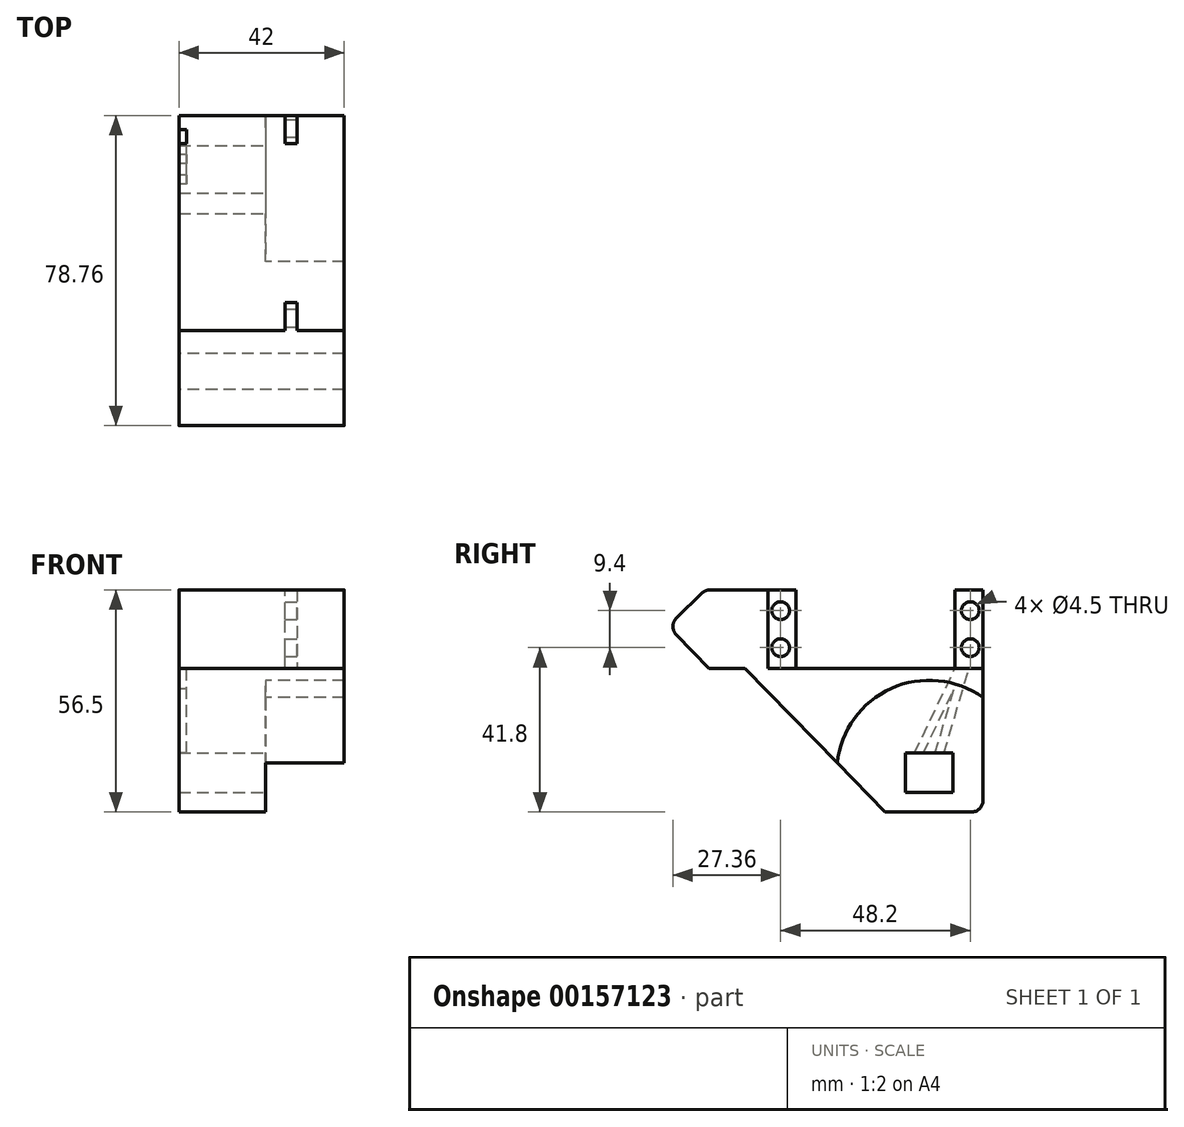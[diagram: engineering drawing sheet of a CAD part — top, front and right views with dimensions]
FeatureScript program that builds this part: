
annotation { "Feature Type Name" : "Feature", "Feature Type Description" : "" }
export const myFeature = defineFeature(function(context is Context, id is Id, definition is map)
    precondition{}
    {
        {
            var Q0;
            Q0=qCreatedBy(makeId("Right.planeOp"),FACE);
            var sketch = newSketch(context, id + "F0", { "sketchPlane" : qUnion([Q0])});
            skLineSegment(sketch, "E0", {"start": v(27.3, -32.2) * mm, "end": v(27.3, 1.3) * mm});
            skLineSegment(sketch, "E1.bottom", {"start": v(19.65, -20.2) * mm, "end": v(7.65, -20.2) * mm});
            skLineSegment(sketch, "E1.top", {"start": v(19.65, -30.2) * mm, "end": v(7.65, -30.2) * mm});
            skLineSegment(sketch, "E1.left", {"start": v(19.65, -20.2) * mm, "end": v(19.65, -30.2) * mm});
            skLineSegment(sketch, "E1.right", {"start": v(7.65, -20.2) * mm, "end": v(7.65, -30.2) * mm});
            skLineSegment(sketch, "E2", {"start": v(7.65, -20.2) * mm, "end": v(19.65, -30.2) * mm, "construction": true});
            skLineSegment(sketch, "E3", {"start": v(13.65, -30.2) * mm, "end": v(13.65, -35.2) * mm, "construction": true});
            skLineSegment(sketch, "E4", {"start": v(27.3, 1.3) * mm, "end": v(27.3, 1.3) * mm});
            skPoint(sketch, "E5.endSnap0", {"position": v(13.65, -32.7) * mm});
            skCircle(sketch, "E6", {"center": v(13.65, -25.2) * mm, "radius": 21.5 * mm, "construction": true});
            skPoint(sketch, "E7.visualSharp", {"position": v(27.3, -35.2) * mm});
            skArc(sketch, "E7.filletArc", {"start": v(24.3, -35.2) * mm, "mid": v(26.42, -34.33) * mm, "end": v(27.3, -32.2) * mm});
            skArc(sketch, "E8", {"start": v(27.3, -6.08) * mm, "mid": v(4, -3.78) * mm, "end": v(-9.72, -22.76) * mm});
            skPoint(sketch, "E9.MirrorCS.end.orphan", {"position": v(0, -6) * mm});
            skLineSegment(sketch, "E10", {"start": v(-27.3, 1.3) * mm, "end": v(27.3, 1.3) * mm});
            skLineSegment(sketch, "E11", {"start": v(7.65, -20.2) * mm, "end": v(13.65, -20.2) * mm, "construction": true});
            skLineSegment(sketch, "E12", {"start": v(13.65, -20.2) * mm, "end": v(13.65, 1.3) * mm, "construction": true});
            skLineSegment(sketch, "E13", {"start": v(13.65, 1.3) * mm, "end": v(13.65, -1.7) * mm, "construction": true});
            skLineSegment(sketch, "E14", {"start": v(27.3, 1.3) * mm, "end": v(20.2, 1.3) * mm});
            skLineSegment(sketch, "E15", {"start": v(20.2, 1.3) * mm, "end": v(20.2, 21.3) * mm});
            skLineSegment(sketch, "E16", {"start": v(20.2, 21.3) * mm, "end": v(27.3, 21.3) * mm});
            skLineSegment(sketch, "E17", {"start": v(27.3, 21.3) * mm, "end": v(27.3, 1.3) * mm});
            skLineSegment(sketch, "E18", {"start": v(-27.3, 1.3) * mm, "end": v(-27.3, 21.3) * mm});
            skLineSegment(sketch, "E19", {"start": v(-27.3, 21.3) * mm, "end": v(-20.2, 21.3) * mm});
            skLineSegment(sketch, "E20", {"start": v(-20.2, 21.3) * mm, "end": v(-20.2, 1.3) * mm});
            skLineSegment(sketch, "E21", {"start": v(-20.2, 1.3) * mm, "end": v(-27.3, 1.3) * mm});
            skLineSegment(sketch, "E22", {"start": v(-20.2, 1.3) * mm, "end": v(-24.1, 1.3) * mm, "construction": true});
            skLineSegment(sketch, "E23", {"start": v(-24.1, 1.3) * mm, "end": v(-24.1, 21.3) * mm, "construction": true});
            skLineSegment(sketch, "E24", {"start": v(20.2, 1.3) * mm, "end": v(24.1, 1.3) * mm, "construction": true});
            skLineSegment(sketch, "E25", {"start": v(24.1, 1.3) * mm, "end": v(24.1, 21.3) * mm, "construction": true});
            skLineSegment(sketch, "E26", {"start": v(-24.1, 1.3) * mm, "end": v(-24.1, 6.6) * mm, "construction": true});
            skLineSegment(sketch, "E27", {"start": v(-24.1, 6.6) * mm, "end": v(-24.1, 16) * mm, "construction": true});
            skLineSegment(sketch, "E28", {"start": v(24.1, 1.3) * mm, "end": v(24.1, 6.6) * mm, "construction": true});
            skLineSegment(sketch, "E29", {"start": v(24.1, 6.6) * mm, "end": v(24.1, 16) * mm, "construction": true});
            skCircle(sketch, "E30", {"center": v(-24.1, 16) * mm, "radius": 2.25 * mm});
            skCircle(sketch, "E31", {"center": v(-24.1, 6.6) * mm, "radius": 2.25 * mm});
            skCircle(sketch, "E32", {"center": v(24.1, 6.6) * mm, "radius": 2.25 * mm});
            skCircle(sketch, "E33", {"center": v(24.1, 16) * mm, "radius": 2.25 * mm});
            skLineSegment(sketch, "E34", {"start": v(24.3, -35.2) * mm, "end": v(2.43, -35.2) * mm});
            skLineSegment(sketch, "E35", {"start": v(20.2, 21.3) * mm, "end": v(10.1, 21.3) * mm, "construction": true});
            skLineSegment(sketch, "E36", {"start": v(10.1, 21.3) * mm, "end": v(10.1, 1.3) * mm, "construction": true});
            skLineSegment(sketch, "E37", {"start": v(-24.1, 11.3) * mm, "end": v(24.1, 11.3) * mm, "construction": true});
            skLineSegment(sketch, "E38", {"start": v(13.65, -35.2) * mm, "end": v(13.65, -46.7) * mm, "construction": true});
            skLineSegment(sketch, "E39", {"start": v(-33.19, 1.3) * mm, "end": v(2.43, -35.2) * mm});
            skLineSegment(sketch, "E40", {"start": v(-27.3, 1.3) * mm, "end": v(-42.25, 1.3) * mm});
            skLineSegment(sketch, "E41", {"start": v(-42.25, 1.3) * mm, "end": v(13.2, -55.54) * mm, "construction": true});
            skPoint(sketch, "E42.second.point", {"position": v(-2.1, -5.74) * mm});
            skPoint(sketch, "E42.third.point", {"position": v(-11.7, -30.01) * mm});
            skArc(sketch, "E43.trimOffspring", {"start": v(-14.8, -17.55) * mm, "mid": v(-10.87, -30.94) * mm, "end": v(2.43, -35.2) * mm});
            skLineSegment(sketch, "E44", {"start": v(-27.3, 21.3) * mm, "end": v(-41.96, 21.3) * mm});
            skLineSegment(sketch, "E45", {"start": v(-42.25, 1.3) * mm, "end": v(-50.6, 9.86) * mm});
            skLineSegment(sketch, "E46", {"start": v(-50.55, 14.1) * mm, "end": v(-44.06, 20.44) * mm});
            skLineSegment(sketch, "E47", {"start": v(-33.19, 1.3) * mm, "end": v(-47.94, 16.41) * mm});
            skPoint(sketch, "E48.visualSharp", {"position": v(-43.18, 21.3) * mm});
            skArc(sketch, "E48.filletArc", {"start": v(-41.96, 21.3) * mm, "mid": v(-43.1, 21.07) * mm, "end": v(-44.06, 20.44) * mm});
            skPoint(sketch, "E49.visualSharp", {"position": v(-52.7, 12) * mm});
            skArc(sketch, "E49.filletArc", {"start": v(-50.55, 14.1) * mm, "mid": v(-51.46, 11.99) * mm, "end": v(-50.6, 9.86) * mm});
            skSolve(sketch);
        }
        {
            var Q0;
            {var subQ6=sQuery(id+"F0.wireOp",EDGE,"E8");Q0=makeQuery(id+"F0.imprint","IMPRINT",FACE,{"disambiguationData":[TD([[makeQuery(id+"F0.imprint","IMPRINT",EDGE,{"derivedFrom":subQ6}),-1.0]])]});}
            var Q1;
            {var subQ2=sQuery(id+"F0.wireOp",EDGE,"E18");Q1=makeQuery(id+"F0.imprint","IMPRINT",FACE,{"disambiguationData":[TD([[makeQuery(id+"F0.imprint","IMPRINT",EDGE,{"derivedFrom":subQ2}),1.0]])]});}
            extrude(context, id + "F1", {"entities" : qUnion([Q0, Q1]), "depth" : 20 * mm});
        }
        {
            var Q0;
            {var subQ6=sQuery(id+"F0.wireOp",EDGE,"E8");Q0=makeQuery(id+"F0.imprint","IMPRINT",FACE,{"disambiguationData":[TD([[makeQuery(id+"F0.imprint","IMPRINT",EDGE,{"derivedFrom":subQ6}),-1.0]])]});}
            var Q1;
            Q1=makeQuery(id+"F0.imprint","IMPRINT",FACE,{"disambiguationData":[TD([[makeQuery(id+"F0.imprint","IMPRINT",EDGE,{"derivedFrom":sQuery(id+"F0.wireOp",EDGE,"E1.bottom")}),-1.0]])]});
            var Q2;
            {var subQ2=sQuery(id+"F0.wireOp",EDGE,"E18");Q2=makeQuery(id+"F0.imprint","IMPRINT",FACE,{"disambiguationData":[TD([[makeQuery(id+"F0.imprint","IMPRINT",EDGE,{"derivedFrom":subQ2}),1.0]])]});}
            extrude(context, id + "F2", {"entities" : qUnion([Q0, Q1, Q2]), "operationType" : NewBodyOperationType.ADD, "oppositeDirection" : true, "depth" : 20 * mm});
        }
        {
            var Q0;
            Q0=makeQuery(id+"F2.opExtrude","CAP_FACE",FACE,{"disambiguationData":[OSD([sQuery(id+"F0.wireOp",EDGE,"E0"),sQuery(id+"F0.wireOp",EDGE,"E1.bottom"),sQuery(id+"F0.wireOp",EDGE,"E1.top"),sQuery(id+"F0.wireOp",EDGE,"E1.left"),sQuery(id+"F0.wireOp",EDGE,"E1.right"),sQuery(id+"F0.wireOp",EDGE,"E7.filletArc"),sQuery(id+"F0.wireOp",EDGE,"E10"),sQuery(id+"F0.wireOp",EDGE,"E14"),sQuery(id+"F0.wireOp",EDGE,"E18"),sQuery(id+"F0.wireOp",EDGE,"E21"),sQuery(id+"F0.wireOp",EDGE,"E34"),sQuery(id+"F0.wireOp",EDGE,"Nva1be2E-KNAd-LMN7-Fm0M-Tev44zCaLiBh"),sQuery(id+"F0.wireOp",EDGE,"E39"),sQuery(id+"F0.wireOp",EDGE,"xTKFIYey-ZxMZ-6zIN-Clns-HEuuajznrW0n"),sQuery(id+"F0.wireOp",EDGE,"E40"),sQuery(id+"F0.wireOp",EDGE,"7Onhy3Lj-w6oU-KviF-Unfc-9GFb9hkfj7ZY")])],"isStart":false});
            var sketch = newSketch(context, id + "F3", { "sketchPlane" : qUnion([Q0])});
            skLineSegment(sketch, "E50.0", {"start": v(-19.65, -20.2) * mm, "end": v(-7.65, -20.2) * mm});
            skLineSegment(sketch, "E50.1", {"start": v(-19.65, -20.2) * mm, "end": v(-19.65, -30.2) * mm});
            skLineSegment(sketch, "E50.2", {"start": v(-7.65, -20.2) * mm, "end": v(-7.65, -30.2) * mm});
            skLineSegment(sketch, "E50.3", {"start": v(-19.65, -30.2) * mm, "end": v(-7.65, -30.2) * mm});
            skLineSegment(sketch, "E51", {"start": v(-13.65, -20.2) * mm, "end": v(-12.15, -20.2) * mm});
            skLineSegment(sketch, "E52", {"start": v(-12.15, -20.2) * mm, "end": v(-12.15, -30.2) * mm});
            skLineSegment(sketch, "E53", {"start": v(-12.15, -30.2) * mm, "end": v(-15.15, -30.2) * mm});
            skLineSegment(sketch, "E54", {"start": v(-15.15, -30.2) * mm, "end": v(-15.15, -20.2) * mm});
            skArc(sketch, "E55.0", {"start": v(14.8, -17.55) * mm, "mid": v(10.87, -30.94) * mm, "end": v(-2.43, -35.2) * mm});
            skSolve(sketch);
        }
        {
            var Q0;
            {var subQ0=sQuery(id+"F3.wireOp",EDGE,"E55.0");Q0=makeQuery(id+"F3.imprint","IMPRINT",FACE,{"disambiguationData":[TD([[makeQuery(id+"F3.imprint","IMPRINT",EDGE,{"derivedFrom":subQ0}),-1.0]])]});}
            var Q1;
            {var subQ0=sQuery(id+"F3.wireOp",EDGE,"E51");Q1=makeQuery(id+"F3.imprint","IMPRINT",FACE,{"disambiguationData":[TD([[makeQuery(id+"F3.imprint","IMPRINT",EDGE,{"derivedFrom":subQ0}),-1.0]])]});}
            var Q2;
            {var subQ5=sQuery(id+"F3.wireOp",EDGE,"E50.1");Q2=makeQuery(id+"F3.imprint","IMPRINT",FACE,{"disambiguationData":[TD([[makeQuery(id+"F3.imprint","IMPRINT",EDGE,{"derivedFrom":subQ5}),-1.0]])]});}
            extrude(context, id + "F4", {"entities" : qUnion([Q0, Q1, Q2]), "operationType" : NewBodyOperationType.ADD, "depth" : 2 * mm});
        }
        {
            var Q0;
            Q0=makeQuery(id+"F1.opExtrude","CAP_FACE",FACE,{"disambiguationData":[OSD([sQuery(id+"F0.wireOp",EDGE,"E0"),sQuery(id+"F0.wireOp",EDGE,"E8"),sQuery(id+"F0.wireOp",EDGE,"E10"),sQuery(id+"F0.wireOp",EDGE,"E14"),sQuery(id+"F0.wireOp",EDGE,"E18"),sQuery(id+"F0.wireOp",EDGE,"E21"),sQuery(id+"F0.wireOp",EDGE,"Nva1be2E-KNAd-LMN7-Fm0M-Tev44zCaLiBh"),sQuery(id+"F0.wireOp",EDGE,"E39"),sQuery(id+"F0.wireOp",EDGE,"xTKFIYey-ZxMZ-6zIN-Clns-HEuuajznrW0n"),sQuery(id+"F0.wireOp",EDGE,"E40"),sQuery(id+"F0.wireOp",EDGE,"7Onhy3Lj-w6oU-KviF-Unfc-9GFb9hkfj7ZY")])],"isStart":false});
            var sketch = newSketch(context, id + "F5", { "sketchPlane" : qUnion([Q0])});
            skSolve(sketch);
        }
        {
            var Q0;
            Q0=makeQuery(id+"F5.imprint","IMPRINT",FACE,{"disambiguationData":[TD([[makeQuery(id+"F5.imprint","IMPRINT",EDGE,{"derivedFrom":makeQuery(id+"F1.opExtrude","CAP_EDGE",EDGE,{"disambiguationData":[OSD([sQuery(id+"F0.wireOp",EDGE,"E0")])],"isStart":false})}),1.0]])]});
            cPlane(context, id + "F6", {"entities" : qUnion([Q0]), "cplaneType" : CPlaneType.OFFSET, "offset" : 12 * mm, "oppositeDirection" : true, "width" : 150 * mm, "height" : 150 * mm});
        }
        {
            var Q0;
            Q0=qCreatedBy(id+"F6.planeOp",FACE);
            var sketch = newSketch(context, id + "F7", { "sketchPlane" : qUnion([Q0])});
            skLineSegment(sketch, "E56.0.0", {"start": v(-27.3, 21.3) * mm, "end": v(-27.3, 1.3) * mm});
            skLineSegment(sketch, "E56.0.1", {"start": v(-27.3, 1.3) * mm, "end": v(-20.2, 1.3) * mm});
            skLineSegment(sketch, "E56.0.2", {"start": v(-20.2, 1.3) * mm, "end": v(-20.2, 21.3) * mm});
            skLineSegment(sketch, "E56.0.3", {"start": v(-20.2, 21.3) * mm, "end": v(-27.3, 21.3) * mm});
            skLineSegment(sketch, "E57.0.0", {"start": v(20.2, 1.3) * mm, "end": v(27.3, 1.3) * mm});
            skLineSegment(sketch, "E57.0.1", {"start": v(27.3, 1.3) * mm, "end": v(27.3, 21.3) * mm});
            skLineSegment(sketch, "E57.0.2", {"start": v(27.3, 21.3) * mm, "end": v(20.2, 21.3) * mm});
            skLineSegment(sketch, "E57.0.3", {"start": v(20.2, 21.3) * mm, "end": v(20.2, 1.3) * mm});
            skLineSegment(sketch, "E58.0", {"start": v(-24.1, 1.3) * mm, "end": v(-24.1, 21.3) * mm});
            skCircle(sketch, "E58.1", {"center": v(-24.1, 16) * mm, "radius": 2.25 * mm});
            skCircle(sketch, "E58.2", {"center": v(-24.1, 6.6) * mm, "radius": 2.25 * mm});
            skLineSegment(sketch, "E58.3", {"start": v(24.1, 1.3) * mm, "end": v(24.1, 21.3) * mm});
            skCircle(sketch, "E58.4", {"center": v(24.1, 6.6) * mm, "radius": 2.25 * mm});
            skCircle(sketch, "E58.5", {"center": v(24.1, 16) * mm, "radius": 2.25 * mm});
            skSolve(sketch);
        }
        {
            var Q0;
            Q0=qSketchRegion(id+"F7",true);
            extrude(context, id + "F8", {"entities" : qUnion([Q0]), "operationType" : NewBodyOperationType.ADD, "oppositeDirection" : true, "depth" : 3 * mm});
        }
        {
            var Q0;
            Q0=makeQuery(id+"F4.opExtrude","CAP_FACE",FACE,{"disambiguationData":[OSD([sQuery(id+"F0.wireOp",EDGE,"E0"),sQuery(id+"F0.wireOp",EDGE,"E7.filletArc"),sQuery(id+"F0.wireOp",EDGE,"E10"),sQuery(id+"F0.wireOp",EDGE,"E14"),sQuery(id+"F0.wireOp",EDGE,"E18"),sQuery(id+"F0.wireOp",EDGE,"E21"),sQuery(id+"F0.wireOp",EDGE,"E34"),sQuery(id+"F0.wireOp",EDGE,"E39"),sQuery(id+"F0.wireOp",EDGE,"E40"),sQuery(id+"F0.wireOp",EDGE,"E44"),sQuery(id+"F0.wireOp",EDGE,"E45"),sQuery(id+"F0.wireOp",EDGE,"E46"),sQuery(id+"F0.wireOp",EDGE,"E48.filletArc"),sQuery(id+"F0.wireOp",EDGE,"E49.filletArc"),sQuery(id+"F3.wireOp",EDGE,"E50.0"),sQuery(id+"F3.wireOp",EDGE,"E50.1"),sQuery(id+"F3.wireOp",EDGE,"E50.2"),sQuery(id+"F3.wireOp",EDGE,"E50.3"),sQuery(id+"F3.wireOp",EDGE,"E52"),sQuery(id+"F3.wireOp",EDGE,"E54"),sQuery(id+"F3.wireOp",EDGE,"E55.0")])],"isStart":false});
            var sketch = newSketch(context, id + "F9", { "sketchPlane" : qUnion([Q0])});
            skLineSegment(sketch, "E59.0", {"start": v(-12.15, -20.2) * mm, "end": v(-9.9, -20.2) * mm});
            skLineSegment(sketch, "E59.1", {"start": v(-17.4, -20.2) * mm, "end": v(-15.15, -20.2) * mm});
            skLineSegment(sketch, "E60.1", {"start": v(-23.75, 1.3) * mm, "end": v(-20.2, 1.3) * mm});
            skLineSegment(sketch, "E61", {"start": v(-9.9, -20.2) * mm, "end": v(-20.2, 1.3) * mm});
            skLineSegment(sketch, "E62", {"start": v(-12.15, -20.2) * mm, "end": v(-19.97, -3.88) * mm});
            skLineSegment(sketch, "E63", {"start": v(-17.4, -20.2) * mm, "end": v(-23.75, 1.3) * mm});
            skLineSegment(sketch, "E64", {"start": v(-15.15, -20.2) * mm, "end": v(-19.97, -3.88) * mm});
            skPoint(sketch, "E65.orphan", {"position": v(27.3, 1.3) * mm});
            skSolve(sketch);
        }
        {
            var Q0;
            Q0=qSketchRegion(id+"F9",true);
            extrude(context, id + "F10", {"entities" : qUnion([Q0]), "operationType" : NewBodyOperationType.REMOVE, "oppositeDirection" : true, "depth" : 2 * mm});
        }
    });
